# Revit family: Stair_Tread-Wooster-Cast_Nosings_Thresholds-101
name_source: partatom
category: Specialty Equipment
revit_build: Autodesk Revit 2017 (Build: 20160720_1515(x64)
units: mm (PartAtom-declared; Revit-internal decimal feet)

## family parameters
Cut with Voids When Loaded = No
Host = Face
OmniClass Number = 23.30.70.21.11.11.11
OmniClass Title = Stair Nosings
Part Type = Normal
Room Calculation Point = No
Round Connector Dimension = Use Diameter
Shared = No

## types (3) — shared parameters
Construction Type = New Construction
Default Elevation = 0' - 0"
Depth = 0' - 0 5/16"
Description = Anti-Slip Stair Nosing
Manufacturer = Wooster Productions Inc
Manufacturer Fax Number = 330-262-4151
Product Documentation Link = http://www.woosterproducts.com
Product Name = Abrasive Cast Nosings
Product Page URL = http://www.woosterproducts.com
URL = http://www.wooster-products.com
Version = 2017 - v2.0a

## per-type parameters (varying)
| type | Width |
| 101-3 | 0' - 3" |
| 101-4 | 0' - 4" |
| 101-6 | 0' - 6" |

note: column(s) folded — value = type name in every type: Model

## geometry (parser evidence)
native form markers: Blend x14, Sweep x8
no freeform markers — native parametric forms only
